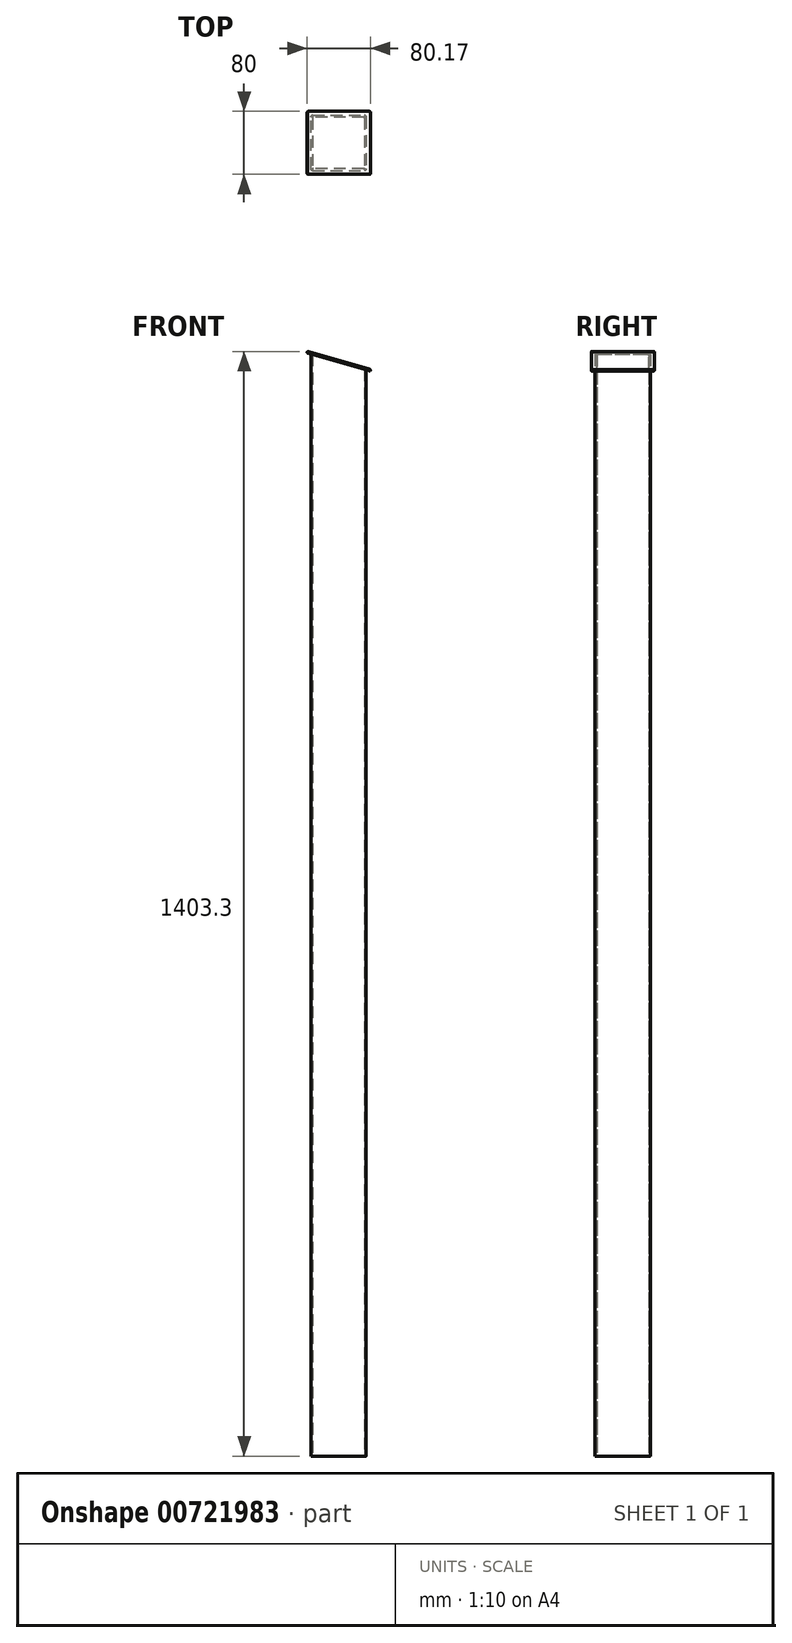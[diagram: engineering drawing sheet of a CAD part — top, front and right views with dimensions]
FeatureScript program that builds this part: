
annotation { "Feature Type Name" : "Feature", "Feature Type Description" : "" }
export const myFeature = defineFeature(function(context is Context, id is Id, definition is map)
    precondition{}
    {
        {
            var Q0;
            Q0=qCreatedBy(makeId("Top.planeOp"),FACE);
            var sketch = newSketch(context, id + "F0", { "sketchPlane" : qUnion([Q0])});
            skLineSegment(sketch, "E0.bottom", {"start": v(-33, -35) * mm, "end": v(33, -35) * mm});
            skLineSegment(sketch, "E0.top", {"start": v(-33, 35) * mm, "end": v(33, 35) * mm});
            skLineSegment(sketch, "E0.left", {"start": v(-35, -33) * mm, "end": v(-35, 33) * mm});
            skLineSegment(sketch, "E0.right", {"start": v(35, -33) * mm, "end": v(35, 33) * mm});
            skPoint(sketch, "E0.middle", {"position": v(0, 0) * mm});
            skLineSegment(sketch, "E1.bottom", {"start": v(-32, -33) * mm, "end": v(32, -33) * mm});
            skLineSegment(sketch, "E1.top", {"start": v(-32, 33) * mm, "end": v(32, 33) * mm});
            skLineSegment(sketch, "E1.left", {"start": v(-33, -32) * mm, "end": v(-33, 32) * mm});
            skLineSegment(sketch, "E1.right", {"start": v(33, -32) * mm, "end": v(33, 32) * mm});
            skPoint(sketch, "E2.visualSharp", {"position": v(-35, 35) * mm});
            skArc(sketch, "E2.filletArc", {"start": v(-33, 35) * mm, "mid": v(-34.41, 34.41) * mm, "end": v(-35, 33) * mm});
            skPoint(sketch, "E3.visualSharp", {"position": v(35, 35) * mm});
            skArc(sketch, "E3.filletArc", {"start": v(35, 33) * mm, "mid": v(34.41, 34.41) * mm, "end": v(33, 35) * mm});
            skPoint(sketch, "E4.visualSharp", {"position": v(35, -35) * mm});
            skArc(sketch, "E4.filletArc", {"start": v(33, -35) * mm, "mid": v(34.41, -34.41) * mm, "end": v(35, -33) * mm});
            skPoint(sketch, "E5.visualSharp", {"position": v(-35, -35) * mm});
            skArc(sketch, "E5.filletArc", {"start": v(-35, -33) * mm, "mid": v(-34.41, -34.41) * mm, "end": v(-33, -35) * mm});
            skArc(sketch, "E6.filletArc", {"start": v(-32, 33) * mm, "mid": v(-32.7, 32.7) * mm, "end": v(-33, 32) * mm});
            skArc(sketch, "E7.filletArc", {"start": v(33, 32) * mm, "mid": v(32.7, 32.7) * mm, "end": v(32, 33) * mm});
            skArc(sketch, "E8.filletArc", {"start": v(32, -33) * mm, "mid": v(32.7, -32.7) * mm, "end": v(33, -32) * mm});
            skArc(sketch, "E9.filletArc", {"start": v(-33, -32) * mm, "mid": v(-32.7, -32.7) * mm, "end": v(-32, -33) * mm});
            skSolve(sketch);
        }
        {
            var Q0;
            Q0=makeQuery(id+"F0.imprint","IMPRINT",FACE,{"disambiguationData":[TD([[makeQuery(id+"F0.imprint","IMPRINT",EDGE,{"derivedFrom":sQuery(id+"F0.wireOp",EDGE,"E0.bottom")}),1.0]])]});
            extrude(context, id + "F1", {"entities" : qUnion([Q0]), "depth" : 1400 * mm, "offsetDistance" : 25 * mm});
        }
        {
            var Q0;
            Q0=qCreatedBy(makeId("Front.planeOp"),FACE);
            var sketch = newSketch(context, id + "F2", { "sketchPlane" : qUnion([Q0])});
            skLineSegment(sketch, "E10", {"start": v(35, 1380) * mm, "end": v(35, 1400) * mm});
            skLineSegment(sketch, "E11", {"start": v(35, 1400) * mm, "end": v(-35, 1400) * mm});
            skLineSegment(sketch, "E12", {"start": v(-35, 1400) * mm, "end": v(35, 1380) * mm});
            skSolve(sketch);
        }
        {
            var Q0;
            Q0=makeQuery(id+"F2.imprint","IMPRINT",FACE,{"disambiguationData":[TD([[makeQuery(id+"F2.imprint","IMPRINT",EDGE,{"derivedFrom":sQuery(id+"F2.wireOp",EDGE,"E10")}),1.0]])]});
            extrude(context, id + "F3", {"entities" : qUnion([Q0]), "operationType" : NewBodyOperationType.REMOVE, "oppositeDirection" : true, "depth" : 35 * mm, "offsetDistance" : 25 * mm, "hasSecondDirection" : true, "secondDirectionOppositeDirection" : false, "secondDirectionDepth" : 35 * mm});
        }
        {
            var Q0;
            Q0=makeQuery(id+"F3.boolean.opBoolean","COPY",FACE,{"derivedFrom":makeQuery(id+"F3.opExtrude","SWEPT_FACE",FACE,{"disambiguationData":[OSD([sQuery(id+"F2.wireOp",EDGE,"E12")])]})});
            cPlane(context, id + "F4", {"entities" : qUnion([Q0]), "cplaneType" : CPlaneType.OFFSET, "offset" : 0 * mm, "width" : 150 * mm, "height" : 150 * mm});
        }
        {
            var Q0;
            Q0=qCreatedBy(id+"F4.planeOp",FACE);
            var sketch = newSketch(context, id + "F5", { "sketchPlane" : qUnion([Q0])});
            skLineSegment(sketch, "E13.bottom", {"start": v(-422.26, 40) * mm, "end": v(-341.46, 40) * mm});
            skLineSegment(sketch, "E13.top", {"start": v(-422.26, -40) * mm, "end": v(-341.46, -40) * mm});
            skLineSegment(sketch, "E13.left", {"start": v(-423.26, 39) * mm, "end": v(-423.26, -39) * mm});
            skLineSegment(sketch, "E13.right", {"start": v(-340.46, 39) * mm, "end": v(-340.46, -39) * mm});
            skPoint(sketch, "E14.visualSharp", {"position": v(-423.26, 40) * mm});
            skArc(sketch, "E14.filletArc", {"start": v(-422.26, 40) * mm, "mid": v(-422.97, 39.7) * mm, "end": v(-423.26, 39) * mm});
            skPoint(sketch, "E15.visualSharp", {"position": v(-340.46, 40) * mm});
            skArc(sketch, "E15.filletArc", {"start": v(-340.46, 39) * mm, "mid": v(-340.75, 39.7) * mm, "end": v(-341.46, 40) * mm});
            skPoint(sketch, "E16.visualSharp", {"position": v(-340.46, -40) * mm});
            skArc(sketch, "E16.filletArc", {"start": v(-341.46, -40) * mm, "mid": v(-340.75, -39.7) * mm, "end": v(-340.46, -39) * mm});
            skPoint(sketch, "E17.visualSharp", {"position": v(-423.26, -40) * mm});
            skArc(sketch, "E17.filletArc", {"start": v(-423.26, -39) * mm, "mid": v(-422.97, -39.7) * mm, "end": v(-422.26, -40) * mm});
            skSolve(sketch);
        }
        {
            var Q0;
            Q0=makeQuery(id+"F5.imprint","IMPRINT",FACE,{"disambiguationData":[TD([[makeQuery(id+"F5.imprint","IMPRINT",EDGE,{"derivedFrom":sQuery(id+"F5.wireOp",EDGE,"E13.bottom")}),-1.0]])]});
            extrude(context, id + "F6", {"entities" : qUnion([Q0]), "operationType" : NewBodyOperationType.ADD, "depth" : 2 * mm, "offsetDistance" : 25 * mm});
        }
    });
